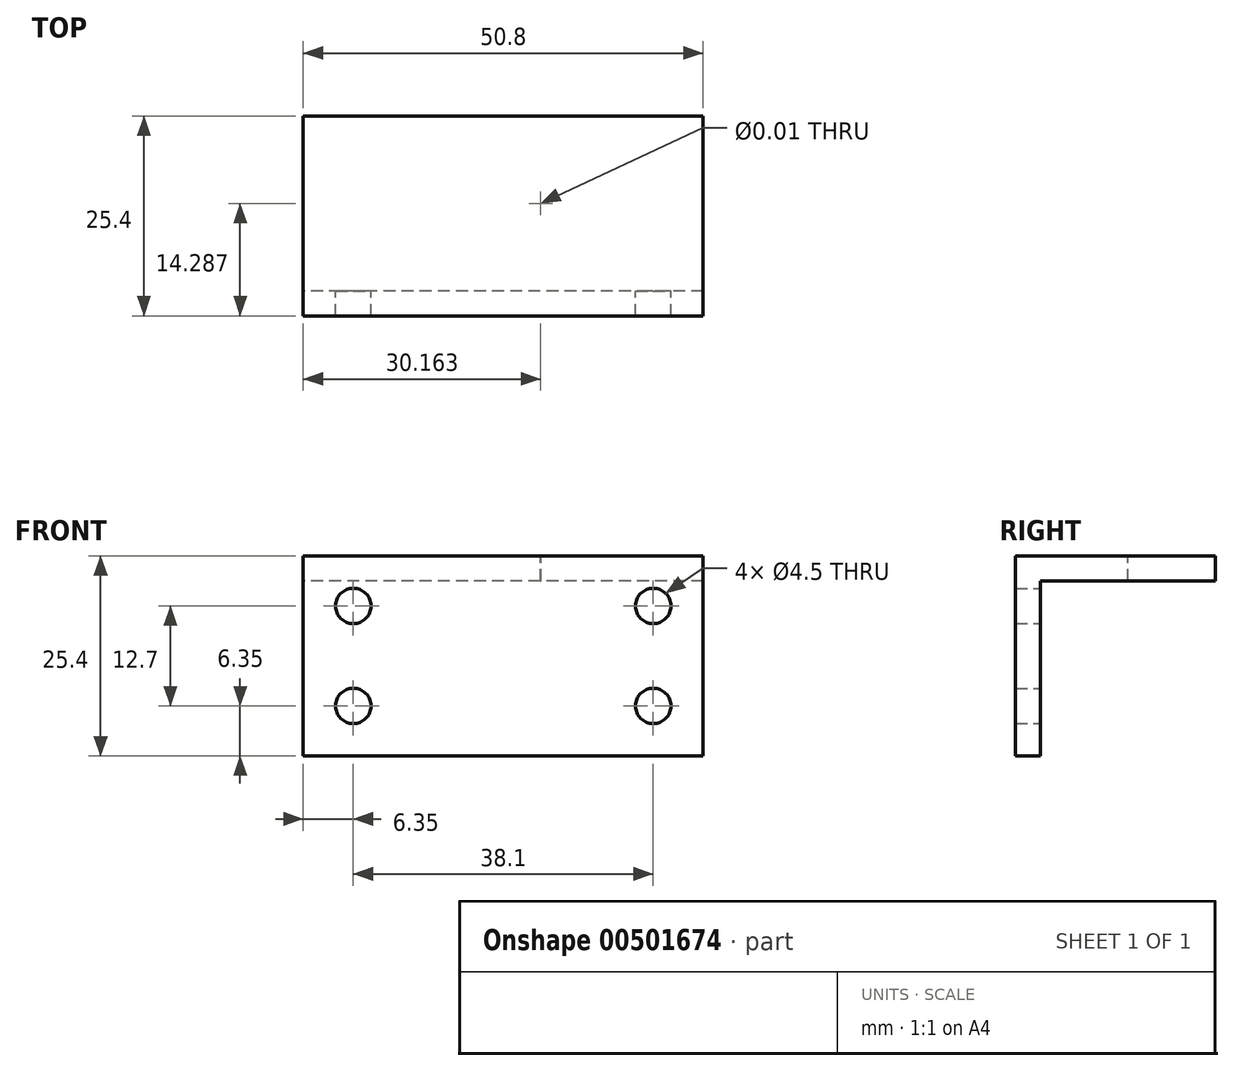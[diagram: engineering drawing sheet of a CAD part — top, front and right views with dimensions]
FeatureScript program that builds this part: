
annotation { "Feature Type Name" : "Feature", "Feature Type Description" : "" }
export const myFeature = defineFeature(function(context is Context, id is Id, definition is map)
    precondition{}
    {
        {
            var Q0;
            Q0=qCreatedBy(makeId("Right.planeOp"),FACE);
            var sketch = newSketch(context, id + "F0", { "sketchPlane" : qUnion([Q0])});
            skLineSegment(sketch, "E0", {"start": v(0, 0) * mm, "end": v(0, 25.4) * mm});
            skLineSegment(sketch, "E1", {"start": v(0, 25.4) * mm, "end": v(25.4, 25.4) * mm});
            skLineSegment(sketch, "E2", {"start": v(25.4, 25.4) * mm, "end": v(25.4, 22.23) * mm});
            skLineSegment(sketch, "E3", {"start": v(25.4, 22.22) * mm, "end": v(3.18, 22.22) * mm});
            skLineSegment(sketch, "E4", {"start": v(3.18, 22.22) * mm, "end": v(3.18, 0) * mm});
            skLineSegment(sketch, "E5", {"start": v(3.18, 0) * mm, "end": v(0, 0) * mm});
            skSolve(sketch);
        }
        {
            var Q0;
            Q0 = qSketchRegion(id + "F0", true);
            extrude(context, id + "F1", {"entities" : qUnion([Q0]), "depth" : 50.8 * mm, "offsetDistance" : 25.4 * mm});
        }
        {
            var Q0;
            Q0=makeQuery(id+"F1.opExtrude","SWEPT_FACE",FACE,{"disambiguationData":[OSD([sQuery(id+"F0.wireOp",EDGE,"E4")])]});
            var sketch = newSketch(context, id + "F2", { "sketchPlane" : qUnion([Q0])});
            skCircle(sketch, "E6", {"center": v(-44.45, 19.05) * mm, "radius": 1.59 * mm});
            skCircle(sketch, "E7", {"center": v(-6.35, 19.05) * mm, "radius": 1.59 * mm});
            skCircle(sketch, "E8", {"center": v(-44.45, 6.35) * mm, "radius": 1.59 * mm});
            skCircle(sketch, "E9", {"center": v(-6.35, 6.35) * mm, "radius": 1.59 * mm});
            skSolve(sketch);
        }
        {
            var Q0;
            Q0=makeQuery(id+"F1.opExtrude","SWEPT_FACE",FACE,{"disambiguationData":[OSD([sQuery(id+"F0.wireOp",EDGE,"E1")])]});
            var sketch = newSketch(context, id + "F3", { "sketchPlane" : qUnion([Q0])});
            skCircle(sketch, "E10", {"center": v(41.28, 14.29) * mm, "radius": 1.79 * mm});
            skPoint(sketch, "E10.centerSnap0", {"position": v(50.8, 14.29) * mm});
            skCircle(sketch, "E11", {"center": v(30.16, 14.29) * mm, "radius": 5.75 * mm});
            skCircle(sketch, "E12", {"center": v(12.7, 14.29) * mm, "radius": 1.79 * mm});
            skSolve(sketch);
        }
        {
            var Q0;
            Q0=sQuery(id+"F2.wireOp",VERTEX,"E8.center");
            var Q1;
            Q1=sQuery(id+"F2.wireOp",VERTEX,"E6.center");
            var Q2;
            Q2=sQuery(id+"F2.wireOp",VERTEX,"E7.center");
            var Q3;
            Q3=sQuery(id+"F2.wireOp",VERTEX,"E9.center");
            var Q4;
            Q4=makeQuery(id+"F1.opExtrude","SWEPT_BODY",BODY,{"disambiguationData":[OSD([sQuery(id+"F0.wireOp",EDGE,"E0"),sQuery(id+"F0.wireOp",EDGE,"E1"),sQuery(id+"F0.wireOp",EDGE,"E2"),sQuery(id+"F0.wireOp",EDGE,"E3"),sQuery(id+"F0.wireOp",EDGE,"E4"),sQuery(id+"F0.wireOp",EDGE,"E5")])]});
            hole(context, id + "F4", {"style" : HoleStyle.SIMPLE, "endStyle" : HoleEndStyle.THROUGH, "standardTappedOrClearance" : lookupTablePath({ "standard" : "ANSI", "fit" : "Normal (ASME)", "size" : "#8", "type" : "Clearance" }), "standardBlindInLast" : lookupTablePath({ "fit" : "Free", "standard" : "ANSI", "size" : "#8", "type" : "Clearance" }), "holeDiameter" : 4.5 * mm, "isTappedThrough" : true, "tappedDepth" : 12.7 * mm, "tapClearance" : 3, "startFromSketch" : true, "locations" : qUnion([Q0, Q1, Q2, Q3]), "scope" : qUnion([Q4])});
        }
        {
            var Q0;
            Q0=sQuery(id+"F3.wireOp",VERTEX,"E11.center");
            var Q1;
            Q1=makeQuery(id+"F1.opExtrude","SWEPT_BODY",BODY,{"disambiguationData":[OSD([sQuery(id+"F0.wireOp",EDGE,"E0"),sQuery(id+"F0.wireOp",EDGE,"E1"),sQuery(id+"F0.wireOp",EDGE,"E2"),sQuery(id+"F0.wireOp",EDGE,"E3"),sQuery(id+"F0.wireOp",EDGE,"E4"),sQuery(id+"F0.wireOp",EDGE,"E5")])]});
            hole(context, id + "F5", {"style" : HoleStyle.SIMPLE, "endStyle" : HoleEndStyle.THROUGH, "standardTappedOrClearance" : lookupTablePath({ "standard" : "ANSI", "size" : "3/8 (0.38)", "type" : "Drilled" }), "standardBlindInLast" : lookupTablePath({ "standard" : "ANSI", "size" : "3/8", "type" : "Drilled" }), "holeDiameter" : 3 / 203.2 * mm, "isTappedThrough" : true, "tappedDepth" : 12.7 * mm, "tapClearance" : 3, "startFromSketch" : true, "locations" : qUnion([Q0]), "scope" : qUnion([Q1])});
        }
    });
